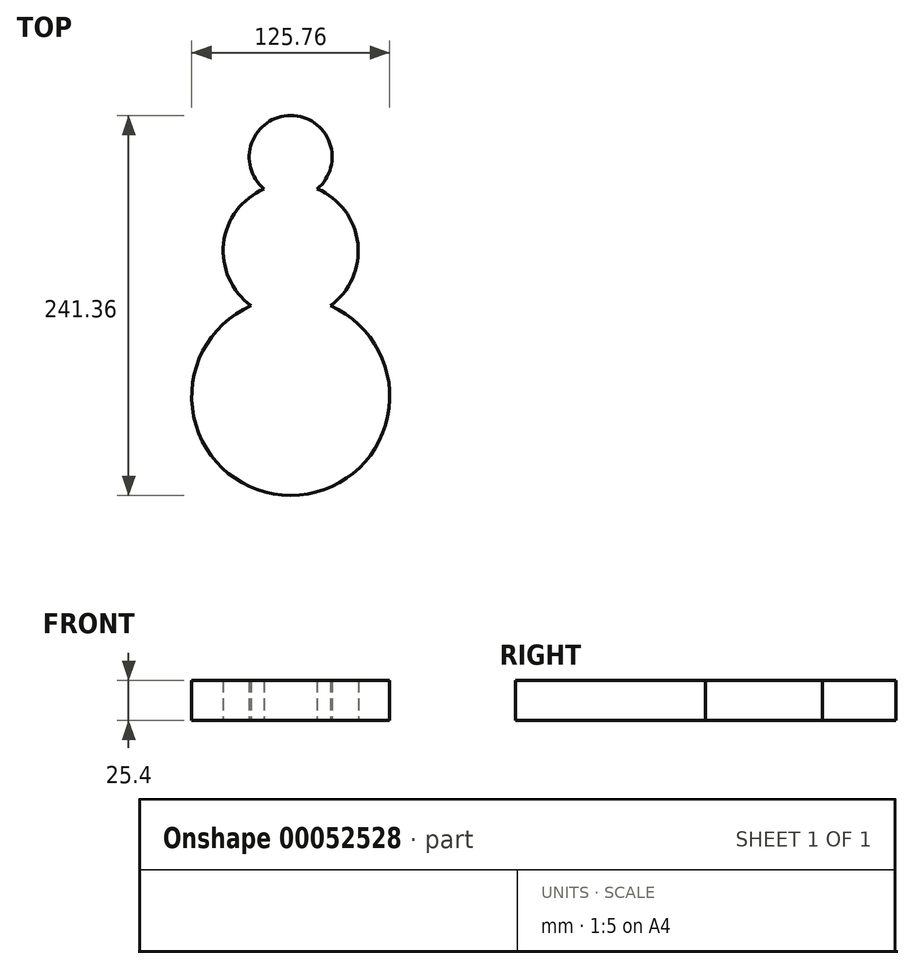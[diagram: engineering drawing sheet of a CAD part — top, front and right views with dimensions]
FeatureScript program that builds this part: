
annotation { "Feature Type Name" : "Feature", "Feature Type Description" : "" }
export const myFeature = defineFeature(function(context is Context, id is Id, definition is map)
    precondition{}
    {
        {
            var Q0;
            Q0=qCreatedBy(makeId("Top.planeOp"),FACE);
            var sketch = newSketch(context, id + "F0", { "sketchPlane" : qUnion([Q0])});
            skCircle(sketch, "E0", {"center": v(0, 0) * mm, "radius": 62.88 * mm});
            skCircle(sketch, "E1", {"center": v(0, 92.41) * mm, "radius": 42.9 * mm});
            skCircle(sketch, "E2", {"center": v(0, 152.14) * mm, "radius": 26.34 * mm});
            skSolve(sketch);
        }
        {
            var Q0;
            Q0 = qSketchRegion(id + "F0", true);
            extrude(context, id + "F1", {"entities" : qUnion([Q0]), "depth" : 25.4 * mm});
        }
    });
